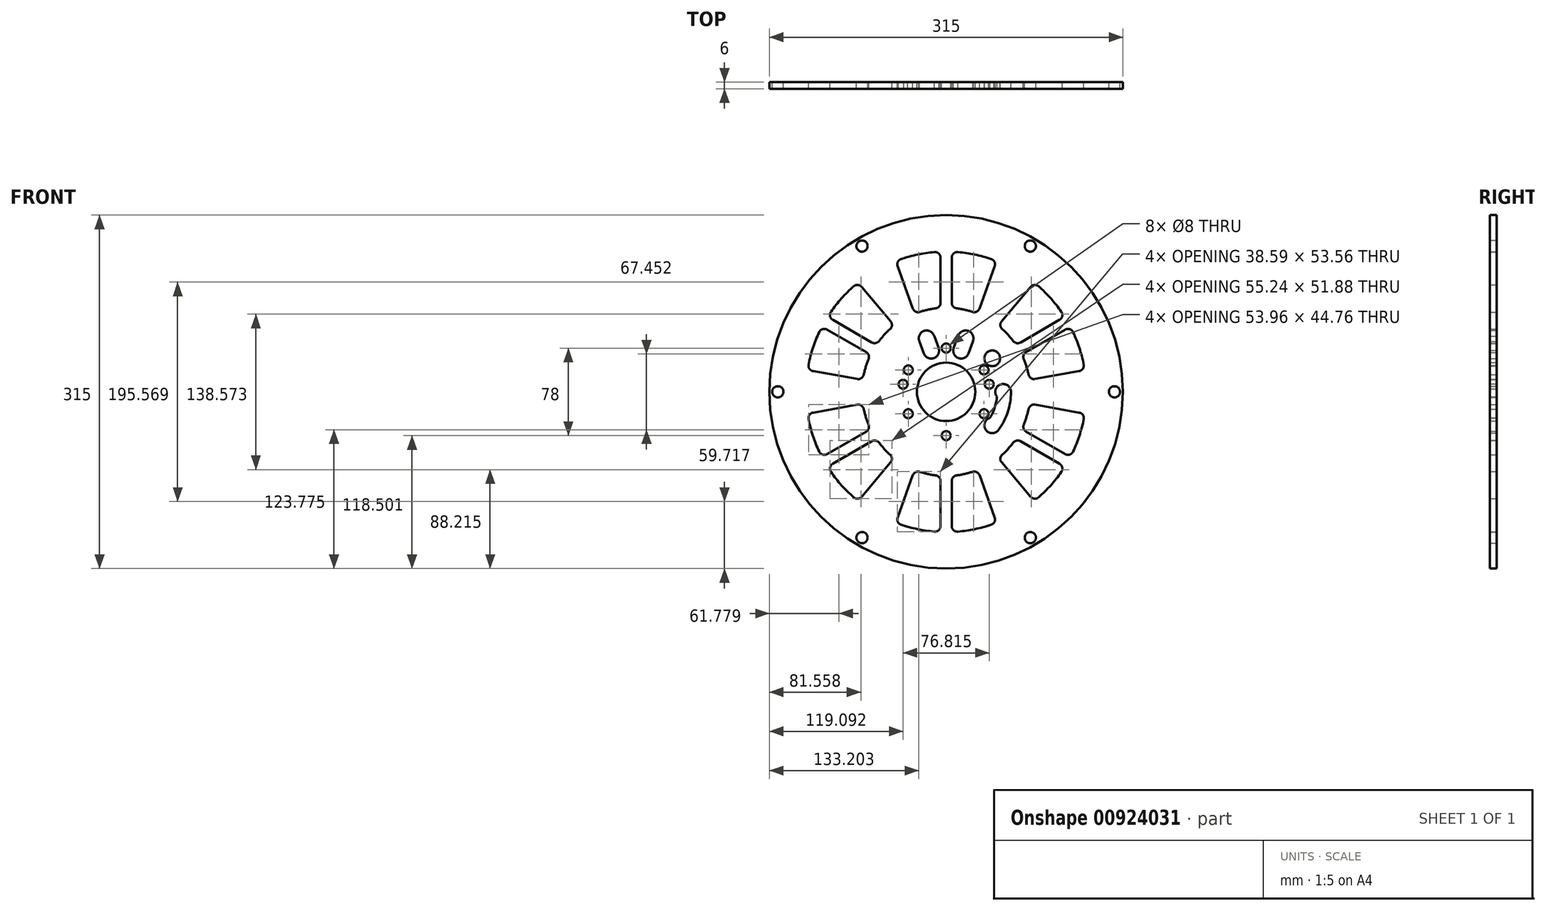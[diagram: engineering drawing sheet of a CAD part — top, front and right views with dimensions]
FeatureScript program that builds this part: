
annotation { "Feature Type Name" : "Feature", "Feature Type Description" : "" }
export const myFeature = defineFeature(function(context is Context, id is Id, definition is map)
    precondition{}
    {
        {
            var Q0;
            Q0=qCreatedBy(makeId("Front.planeOp"),FACE);
            var sketch = newSketch(context, id + "F0", { "sketchPlane" : qUnion([Q0])});
            skCircle(sketch, "E0", {"center": v(-91.13, 167.67) * mm, "radius": 15 * mm, "construction": true});
            skCircle(sketch, "E1", {"center": v(-91.13, 167.67) * mm, "radius": 26 * mm});
            skCircle(sketch, "E2", {"center": v(-91.13, 167.67) * mm, "radius": 39 * mm, "construction": true});
            skCircle(sketch, "E3", {"center": v(-91.13, 167.67) * mm, "radius": 62.5 * mm, "construction": true});
            skCircle(sketch, "E4", {"center": v(-91.13, 167.67) * mm, "radius": 140 * mm, "construction": true});
            skCircle(sketch, "E5", {"center": v(-40.38, 167.67) * mm, "radius": 4.86 * mm, "construction": true});
            skLineSegment(sketch, "E6", {"start": v(-52.13, 167.67) * mm, "end": v(-28.63, 167.67) * mm, "construction": true});
            skCircle(sketch, "E7", {"center": v(-91.13, 167.67) * mm, "radius": 50.75 * mm, "construction": true});
            skCircle(sketch, "E8.1.0", {"center": v(-42.86, 183.35) * mm, "radius": 4.86 * mm, "construction": true});
            skCircle(sketch, "E8.2.0", {"center": v(-50.07, 197.5) * mm, "radius": 4.86 * mm, "construction": true});
            skCircle(sketch, "E8.3.0", {"center": v(-61.3, 208.73) * mm, "radius": 4.86 * mm, "construction": true});
            skCircle(sketch, "E8.4.0", {"center": v(-75.45, 215.94) * mm, "radius": 4.86 * mm, "construction": true});
            skCircle(sketch, "E8.5.0", {"center": v(-91.13, 218.42) * mm, "radius": 4.86 * mm, "construction": true});
            skCircle(sketch, "E8.6.0", {"center": v(-106.81, 215.94) * mm, "radius": 4.86 * mm, "construction": true});
            skCircle(sketch, "E8.7.0", {"center": v(-120.96, 208.73) * mm, "radius": 4.86 * mm, "construction": true});
            skCircle(sketch, "E8.8.0", {"center": v(-132.19, 197.5) * mm, "radius": 4.86 * mm, "construction": true});
            skCircle(sketch, "E8.9.0", {"center": v(-139.4, 183.35) * mm, "radius": 4.86 * mm, "construction": true});
            skCircle(sketch, "E8.10.0", {"center": v(-141.88, 167.67) * mm, "radius": 4.86 * mm, "construction": true});
            skCircle(sketch, "E8.11.0", {"center": v(-139.4, 151.99) * mm, "radius": 4.86 * mm, "construction": true});
            skCircle(sketch, "E8.12.0", {"center": v(-132.19, 137.84) * mm, "radius": 4.86 * mm, "construction": true});
            skCircle(sketch, "E8.13.0", {"center": v(-120.96, 126.61) * mm, "radius": 4.86 * mm, "construction": true});
            skCircle(sketch, "E8.14.0", {"center": v(-106.81, 119.4) * mm, "radius": 4.86 * mm, "construction": true});
            skCircle(sketch, "E8.15.0", {"center": v(-91.13, 116.92) * mm, "radius": 4.86 * mm, "construction": true});
            skCircle(sketch, "E8.16.0", {"center": v(-75.45, 119.4) * mm, "radius": 4.86 * mm, "construction": true});
            skCircle(sketch, "E8.17.0", {"center": v(-61.3, 126.61) * mm, "radius": 4.86 * mm, "construction": true});
            skCircle(sketch, "E8.18.0", {"center": v(-50.07, 137.84) * mm, "radius": 4.86 * mm, "construction": true});
            skCircle(sketch, "E8.19.0", {"center": v(-42.86, 151.99) * mm, "radius": 4.86 * mm, "construction": true});
            skCircle(sketch, "E9", {"center": v(-50.07, 197.5) * mm, "radius": 7 * mm});
            skArc(sketch, "E10", {"start": v(-33.38, 167.67) * mm, "mid": v(-42.7, 174.28) * mm, "end": v(-45.84, 163.3) * mm});
            skArc(sketch, "E11", {"start": v(-51.92, 144.6) * mm, "mid": v(-55.83, 133.86) * mm, "end": v(-44.4, 133.73) * mm});
            skCircle(sketch, "E12", {"center": v(-91.13, 167.67) * mm, "radius": 157.5 * mm});
            skCircle(sketch, "E13", {"center": v(-91.13, 167.67) * mm, "radius": 150 * mm, "construction": true});
            skCircle(sketch, "E14", {"center": v(58.87, 167.67) * mm, "radius": 5 * mm});
            skCircle(sketch, "E15.1.0", {"center": v(-16.13, 297.58) * mm, "radius": 5 * mm});
            skCircle(sketch, "E15.2.0", {"center": v(-166.13, 297.58) * mm, "radius": 5 * mm});
            skCircle(sketch, "E15.3.0", {"center": v(-241.13, 167.67) * mm, "radius": 5 * mm});
            skCircle(sketch, "E15.4.0", {"center": v(-166.13, 37.77) * mm, "radius": 5 * mm});
            skCircle(sketch, "E15.5.0", {"center": v(-16.13, 37.77) * mm, "radius": 5 * mm});
            skCircle(sketch, "E16", {"center": v(-91.13, 206.67) * mm, "radius": 4 * mm});
            skCircle(sketch, "E17.1.0", {"center": v(-104.47, 204.32) * mm, "radius": 4 * mm, "construction": true});
            skCircle(sketch, "E17.2.0", {"center": v(-116.2, 197.55) * mm, "radius": 4 * mm, "construction": true});
            skCircle(sketch, "E17.3.0", {"center": v(-124.9, 187.17) * mm, "radius": 4 * mm});
            skCircle(sketch, "E17.4.0", {"center": v(-129.54, 174.44) * mm, "radius": 4 * mm});
            skCircle(sketch, "E17.5.0", {"center": v(-129.54, 160.9) * mm, "radius": 4 * mm, "construction": true});
            skCircle(sketch, "E17.6.0", {"center": v(-124.9, 148.17) * mm, "radius": 4 * mm});
            skCircle(sketch, "E17.7.0", {"center": v(-116.2, 137.8) * mm, "radius": 4 * mm, "construction": true});
            skCircle(sketch, "E17.8.0", {"center": v(-104.47, 131.02) * mm, "radius": 4 * mm, "construction": true});
            skCircle(sketch, "E17.9.0", {"center": v(-91.13, 128.67) * mm, "radius": 4 * mm});
            skCircle(sketch, "E17.10.0", {"center": v(-77.8, 131.02) * mm, "radius": 4 * mm, "construction": true});
            skCircle(sketch, "E17.11.0", {"center": v(-66.06, 137.8) * mm, "radius": 4 * mm, "construction": true});
            skCircle(sketch, "E17.12.0", {"center": v(-57.36, 148.17) * mm, "radius": 4 * mm});
            skCircle(sketch, "E17.13.0", {"center": v(-52.72, 160.9) * mm, "radius": 4 * mm, "construction": true});
            skCircle(sketch, "E17.14.0", {"center": v(-52.72, 174.44) * mm, "radius": 4 * mm});
            skCircle(sketch, "E17.15.0", {"center": v(-57.36, 187.17) * mm, "radius": 4 * mm});
            skCircle(sketch, "E17.16.0", {"center": v(-66.06, 197.55) * mm, "radius": 4 * mm, "construction": true});
            skCircle(sketch, "E17.17.0", {"center": v(-77.8, 204.32) * mm, "radius": 4 * mm, "construction": true});
            skArc(sketch, "E18", {"start": v(-105.73, 211.2) * mm, "mid": v(-105.85, 211.18) * mm, "end": v(-105.98, 211.15) * mm});
            skCircle(sketch, "E19", {"center": v(-91.13, 167.67) * mm, "radius": 134 * mm, "construction": true});
            skArc(sketch, "E20", {"start": v(-50.92, 49.31) * mm, "mid": v(-91.13, 292.67) * mm, "end": v(-131.34, 49.31) * mm, "construction": true});
            skCircle(sketch, "E21", {"center": v(-91.13, 167.67) * mm, "radius": 75 * mm, "construction": true});
            skLineSegment(sketch, "E22", {"start": v(-304.88, 167.67) * mm, "end": v(220.89, 167.67) * mm, "construction": true});
            skLineSegment(sketch, "E23", {"start": v(-166.13, 37.77) * mm, "end": v(-16.13, 297.58) * mm, "construction": true});
            skLineSegment(sketch, "E24", {"start": v(-166.13, 297.58) * mm, "end": v(-16.13, 37.77) * mm, "construction": true});
            skArc(sketch, "E25", {"start": v(-114.57, 96.43) * mm, "mid": v(-107.61, 94.5) * mm, "end": v(-100.5, 93.26) * mm});
            skArc(sketch, "E26", {"start": v(-131.34, 49.31) * mm, "mid": v(-116.63, 45.3) * mm, "end": v(-101.55, 43.1) * mm});
            skLineSegment(sketch, "E27", {"start": v(-120.83, 93.38) * mm, "end": v(-134.43, 55.75) * mm});
            skLineSegment(sketch, "E28", {"start": v(-61.43, 93.38) * mm, "end": v(-47.83, 55.75) * mm});
            skLineSegment(sketch, "E29", {"start": v(-91.13, 42.67) * mm, "end": v(-91.13, 92.67) * mm, "construction": true});
            skLineSegment(sketch, "E30", {"start": v(-86.13, 88.3) * mm, "end": v(-86.13, 48.09) * mm});
            skLineSegment(sketch, "E31", {"start": v(-96.13, 88.3) * mm, "end": v(-96.13, 48.09) * mm});
            skArc(sketch, "E32.trimOffspring", {"start": v(-81.76, 93.26) * mm, "mid": v(-74.65, 94.5) * mm, "end": v(-67.7, 96.43) * mm});
            skArc(sketch, "E33.trimOffspring", {"start": v(-80.71, 43.1) * mm, "mid": v(-65.63, 45.3) * mm, "end": v(-50.92, 49.31) * mm});
            skPoint(sketch, "E34.visualSharp", {"position": v(-46.13, 51.05) * mm});
            skArc(sketch, "E34.filletArc", {"start": v(-50.92, 49.31) * mm, "mid": v(-48.02, 51.88) * mm, "end": v(-47.83, 55.75) * mm});
            skPoint(sketch, "E35.visualSharp", {"position": v(-63.13, 98.1) * mm});
            skArc(sketch, "E35.filletArc", {"start": v(-61.43, 93.38) * mm, "mid": v(-63.94, 96.17) * mm, "end": v(-67.7, 96.43) * mm});
            skPoint(sketch, "E36.visualSharp", {"position": v(-119.13, 98.1) * mm});
            skArc(sketch, "E36.filletArc", {"start": v(-114.57, 96.43) * mm, "mid": v(-118.32, 96.17) * mm, "end": v(-120.83, 93.38) * mm});
            skPoint(sketch, "E37.visualSharp", {"position": v(-136.13, 51.05) * mm});
            skArc(sketch, "E37.filletArc", {"start": v(-134.43, 55.75) * mm, "mid": v(-134.24, 51.88) * mm, "end": v(-131.34, 49.31) * mm});
            skPoint(sketch, "E38.visualSharp", {"position": v(-96.13, 92.84) * mm});
            skArc(sketch, "E38.filletArc", {"start": v(-96.13, 88.3) * mm, "mid": v(-97.38, 91.6) * mm, "end": v(-100.5, 93.26) * mm});
            skPoint(sketch, "E39.visualSharp", {"position": v(-96.13, 42.77) * mm});
            skArc(sketch, "E39.filletArc", {"start": v(-101.55, 43.1) * mm, "mid": v(-97.75, 44.4) * mm, "end": v(-96.13, 48.09) * mm});
            skPoint(sketch, "E40.visualSharp", {"position": v(-86.13, 42.77) * mm});
            skArc(sketch, "E40.filletArc", {"start": v(-86.13, 48.09) * mm, "mid": v(-84.52, 44.4) * mm, "end": v(-80.71, 43.1) * mm});
            skPoint(sketch, "E41.visualSharp", {"position": v(-86.13, 92.84) * mm});
            skArc(sketch, "E41.filletArc", {"start": v(-81.76, 93.26) * mm, "mid": v(-84.88, 91.6) * mm, "end": v(-86.13, 88.3) * mm});
            skArc(sketch, "E42.trimOffspring", {"start": v(-101.55, 43.1) * mm, "mid": v(-91.13, 42.67) * mm, "end": v(-80.71, 43.1) * mm, "construction": true});
            skArc(sketch, "E43.1.0", {"start": v(-41.15, 111.75) * mm, "mid": v(-36, 116.81) * mm, "end": v(-31.38, 122.35) * mm});
            skArc(sketch, "E43.1.1", {"start": v(-22, 138.58) * mm, "mid": v(-19.52, 145.36) * mm, "end": v(-17.71, 152.35) * mm});
            skArc(sketch, "E43.1.2", {"start": v(-11.94, 156.25) * mm, "mid": v(-15.62, 155.47) * mm, "end": v(-17.71, 152.35) * mm});
            skArc(sketch, "E43.1.3", {"start": v(-22, 138.58) * mm, "mid": v(-22.13, 135.05) * mm, "end": v(-19.9, 132.32) * mm});
            skArc(sketch, "E43.1.4", {"start": v(-24.9, 123.66) * mm, "mid": v(-28.38, 124.23) * mm, "end": v(-31.38, 122.35) * mm});
            skLineSegment(sketch, "E43.1.5", {"start": v(-24.9, 123.66) * mm, "end": v(9.93, 103.55) * mm});
            skLineSegment(sketch, "E43.1.6", {"start": v(-41.64, 104.8) * mm, "end": v(-15.85, 74.2) * mm});
            skArc(sketch, "E43.1.7", {"start": v(-41.15, 111.75) * mm, "mid": v(-42.8, 108.37) * mm, "end": v(-41.64, 104.8) * mm});
            skArc(sketch, "E43.1.8", {"start": v(-15.85, 74.2) * mm, "mid": v(-12.4, 72.45) * mm, "end": v(-8.73, 73.67) * mm});
            skArc(sketch, "E43.1.9", {"start": v(-8.73, 73.67) * mm, "mid": v(2.1, 84.4) * mm, "end": v(11.54, 96.37) * mm});
            skArc(sketch, "E43.1.10", {"start": v(11.54, 96.37) * mm, "mid": v(12.31, 100.31) * mm, "end": v(9.93, 103.55) * mm});
            skArc(sketch, "E43.1.11", {"start": v(14.93, 112.21) * mm, "mid": v(18.93, 111.77) * mm, "end": v(21.95, 114.4) * mm});
            skLineSegment(sketch, "E43.1.12", {"start": v(-19.9, 132.32) * mm, "end": v(14.93, 112.21) * mm});
            skArc(sketch, "E43.1.13", {"start": v(21.95, 114.4) * mm, "mid": v(27.6, 128.57) * mm, "end": v(31.47, 143.32) * mm});
            skLineSegment(sketch, "E43.1.14", {"start": v(-11.94, 156.25) * mm, "end": v(27.45, 149.21) * mm});
            skArc(sketch, "E43.1.15", {"start": v(31.47, 143.32) * mm, "mid": v(30.7, 147.1) * mm, "end": v(27.45, 149.21) * mm});
            skArc(sketch, "E43.2.0", {"start": v(-17.71, 183) * mm, "mid": v(-19.52, 189.98) * mm, "end": v(-22, 196.76) * mm});
            skArc(sketch, "E43.2.1", {"start": v(-31.38, 213) * mm, "mid": v(-36, 218.53) * mm, "end": v(-41.15, 223.6) * mm});
            skArc(sketch, "E43.2.2", {"start": v(-41.64, 230.54) * mm, "mid": v(-42.8, 226.97) * mm, "end": v(-41.15, 223.6) * mm});
            skArc(sketch, "E43.2.3", {"start": v(-31.38, 213) * mm, "mid": v(-28.38, 211.12) * mm, "end": v(-24.9, 211.69) * mm});
            skArc(sketch, "E43.2.4", {"start": v(-19.9, 203.03) * mm, "mid": v(-22.13, 200.3) * mm, "end": v(-22, 196.76) * mm});
            skLineSegment(sketch, "E43.2.5", {"start": v(-19.9, 203.03) * mm, "end": v(14.93, 223.13) * mm});
            skLineSegment(sketch, "E43.2.6", {"start": v(-11.94, 179.1) * mm, "end": v(27.45, 186.13) * mm});
            skArc(sketch, "E43.2.7", {"start": v(-17.71, 183) * mm, "mid": v(-15.62, 179.87) * mm, "end": v(-11.94, 179.1) * mm});
            skArc(sketch, "E43.2.8", {"start": v(27.45, 186.13) * mm, "mid": v(30.7, 188.23) * mm, "end": v(31.47, 192.03) * mm});
            skArc(sketch, "E43.2.9", {"start": v(31.47, 192.03) * mm, "mid": v(27.6, 206.77) * mm, "end": v(21.95, 220.93) * mm});
            skArc(sketch, "E43.2.10", {"start": v(21.95, 220.93) * mm, "mid": v(18.93, 223.57) * mm, "end": v(14.93, 223.13) * mm});
            skArc(sketch, "E43.2.11", {"start": v(9.93, 231.8) * mm, "mid": v(12.31, 235.03) * mm, "end": v(11.54, 238.98) * mm});
            skLineSegment(sketch, "E43.2.12", {"start": v(-24.9, 211.69) * mm, "end": v(9.93, 231.8) * mm});
            skArc(sketch, "E43.2.13", {"start": v(11.54, 238.98) * mm, "mid": v(2.1, 250.94) * mm, "end": v(-8.73, 261.67) * mm});
            skLineSegment(sketch, "E43.2.14", {"start": v(-41.64, 230.54) * mm, "end": v(-15.85, 261.13) * mm});
            skArc(sketch, "E43.2.15", {"start": v(-8.73, 261.67) * mm, "mid": v(-12.4, 262.9) * mm, "end": v(-15.85, 261.13) * mm});
            skArc(sketch, "E43.3.0", {"start": v(-67.7, 238.91) * mm, "mid": v(-74.65, 240.84) * mm, "end": v(-81.76, 242.08) * mm});
            skArc(sketch, "E43.3.1", {"start": v(-100.5, 242.08) * mm, "mid": v(-107.61, 240.84) * mm, "end": v(-114.57, 238.91) * mm});
            skArc(sketch, "E43.3.2", {"start": v(-120.83, 241.96) * mm, "mid": v(-118.32, 239.17) * mm, "end": v(-114.57, 238.91) * mm});
            skArc(sketch, "E43.3.3", {"start": v(-100.5, 242.08) * mm, "mid": v(-97.38, 243.74) * mm, "end": v(-96.13, 247.04) * mm});
            skArc(sketch, "E43.3.4", {"start": v(-86.13, 247.04) * mm, "mid": v(-84.88, 243.74) * mm, "end": v(-81.76, 242.08) * mm});
            skLineSegment(sketch, "E43.3.5", {"start": v(-86.13, 247.04) * mm, "end": v(-86.13, 287.25) * mm});
            skLineSegment(sketch, "E43.3.6", {"start": v(-61.43, 241.96) * mm, "end": v(-47.83, 279.6) * mm});
            skArc(sketch, "E43.3.7", {"start": v(-67.7, 238.91) * mm, "mid": v(-63.94, 239.17) * mm, "end": v(-61.43, 241.96) * mm});
            skArc(sketch, "E43.3.8", {"start": v(-47.83, 279.6) * mm, "mid": v(-48.02, 283.46) * mm, "end": v(-50.92, 286.03) * mm});
            skArc(sketch, "E43.3.9", {"start": v(-50.92, 286.03) * mm, "mid": v(-65.63, 290.04) * mm, "end": v(-80.71, 292.24) * mm});
            skArc(sketch, "E43.3.10", {"start": v(-80.71, 292.24) * mm, "mid": v(-84.52, 290.93) * mm, "end": v(-86.13, 287.25) * mm});
            skArc(sketch, "E43.3.11", {"start": v(-96.13, 287.25) * mm, "mid": v(-97.75, 290.93) * mm, "end": v(-101.55, 292.24) * mm});
            skLineSegment(sketch, "E43.3.12", {"start": v(-96.13, 247.04) * mm, "end": v(-96.13, 287.25) * mm});
            skArc(sketch, "E43.3.13", {"start": v(-101.55, 292.24) * mm, "mid": v(-116.63, 290.04) * mm, "end": v(-131.34, 286.03) * mm});
            skLineSegment(sketch, "E43.3.14", {"start": v(-120.83, 241.96) * mm, "end": v(-134.43, 279.6) * mm});
            skArc(sketch, "E43.3.15", {"start": v(-131.34, 286.03) * mm, "mid": v(-134.24, 283.46) * mm, "end": v(-134.43, 279.6) * mm});
            skArc(sketch, "E43.4.0", {"start": v(-141.1, 223.6) * mm, "mid": v(-146.25, 218.53) * mm, "end": v(-150.89, 213) * mm});
            skArc(sketch, "E43.4.1", {"start": v(-160.26, 196.76) * mm, "mid": v(-162.74, 189.98) * mm, "end": v(-164.55, 183) * mm});
            skArc(sketch, "E43.4.2", {"start": v(-170.32, 179.1) * mm, "mid": v(-166.64, 179.87) * mm, "end": v(-164.55, 183) * mm});
            skArc(sketch, "E43.4.3", {"start": v(-160.26, 196.76) * mm, "mid": v(-160.13, 200.3) * mm, "end": v(-162.37, 203.03) * mm});
            skArc(sketch, "E43.4.4", {"start": v(-157.37, 211.69) * mm, "mid": v(-153.88, 211.12) * mm, "end": v(-150.89, 213) * mm});
            skLineSegment(sketch, "E43.4.5", {"start": v(-157.37, 211.69) * mm, "end": v(-192.2, 231.8) * mm});
            skLineSegment(sketch, "E43.4.6", {"start": v(-140.62, 230.54) * mm, "end": v(-166.4, 261.13) * mm});
            skArc(sketch, "E43.4.7", {"start": v(-141.1, 223.6) * mm, "mid": v(-139.45, 226.97) * mm, "end": v(-140.62, 230.54) * mm});
            skArc(sketch, "E43.4.8", {"start": v(-166.4, 261.13) * mm, "mid": v(-169.85, 262.9) * mm, "end": v(-173.53, 261.67) * mm});
            skArc(sketch, "E43.4.9", {"start": v(-173.53, 261.67) * mm, "mid": v(-184.36, 250.94) * mm, "end": v(-193.8, 238.98) * mm});
            skArc(sketch, "E43.4.10", {"start": v(-193.8, 238.98) * mm, "mid": v(-194.57, 235.03) * mm, "end": v(-192.2, 231.8) * mm});
            skArc(sketch, "E43.4.11", {"start": v(-197.2, 223.13) * mm, "mid": v(-201.19, 223.57) * mm, "end": v(-204.22, 220.93) * mm});
            skLineSegment(sketch, "E43.4.12", {"start": v(-162.37, 203.03) * mm, "end": v(-197.2, 223.13) * mm});
            skArc(sketch, "E43.4.13", {"start": v(-204.22, 220.93) * mm, "mid": v(-209.86, 206.77) * mm, "end": v(-213.73, 192.03) * mm});
            skLineSegment(sketch, "E43.4.14", {"start": v(-170.32, 179.1) * mm, "end": v(-209.7, 186.13) * mm});
            skArc(sketch, "E43.4.15", {"start": v(-213.73, 192.03) * mm, "mid": v(-212.96, 188.23) * mm, "end": v(-209.7, 186.13) * mm});
            skArc(sketch, "E43.5.0", {"start": v(-164.55, 152.35) * mm, "mid": v(-162.74, 145.36) * mm, "end": v(-160.26, 138.58) * mm});
            skArc(sketch, "E43.5.1", {"start": v(-150.89, 122.35) * mm, "mid": v(-146.25, 116.81) * mm, "end": v(-141.1, 111.75) * mm});
            skArc(sketch, "E43.5.2", {"start": v(-140.62, 104.8) * mm, "mid": v(-139.45, 108.37) * mm, "end": v(-141.1, 111.75) * mm});
            skArc(sketch, "E43.5.3", {"start": v(-150.89, 122.35) * mm, "mid": v(-153.88, 124.23) * mm, "end": v(-157.37, 123.66) * mm});
            skArc(sketch, "E43.5.4", {"start": v(-162.37, 132.32) * mm, "mid": v(-160.13, 135.05) * mm, "end": v(-160.26, 138.58) * mm});
            skLineSegment(sketch, "E43.5.5", {"start": v(-162.37, 132.32) * mm, "end": v(-197.2, 112.21) * mm});
            skLineSegment(sketch, "E43.5.6", {"start": v(-170.32, 156.25) * mm, "end": v(-209.7, 149.21) * mm});
            skArc(sketch, "E43.5.7", {"start": v(-164.55, 152.35) * mm, "mid": v(-166.64, 155.47) * mm, "end": v(-170.32, 156.25) * mm});
            skArc(sketch, "E43.5.8", {"start": v(-209.7, 149.21) * mm, "mid": v(-212.96, 147.1) * mm, "end": v(-213.73, 143.32) * mm});
            skArc(sketch, "E43.5.9", {"start": v(-213.73, 143.32) * mm, "mid": v(-209.86, 128.57) * mm, "end": v(-204.22, 114.4) * mm});
            skArc(sketch, "E43.5.10", {"start": v(-204.22, 114.4) * mm, "mid": v(-201.19, 111.77) * mm, "end": v(-197.2, 112.21) * mm});
            skArc(sketch, "E43.5.11", {"start": v(-192.2, 103.55) * mm, "mid": v(-194.57, 100.31) * mm, "end": v(-193.8, 96.37) * mm});
            skLineSegment(sketch, "E43.5.12", {"start": v(-157.37, 123.66) * mm, "end": v(-192.2, 103.55) * mm});
            skArc(sketch, "E43.5.13", {"start": v(-193.8, 96.37) * mm, "mid": v(-184.36, 84.4) * mm, "end": v(-173.53, 73.67) * mm});
            skLineSegment(sketch, "E43.5.14", {"start": v(-140.62, 104.8) * mm, "end": v(-166.4, 74.2) * mm});
            skArc(sketch, "E43.5.15", {"start": v(-173.53, 73.67) * mm, "mid": v(-169.85, 72.45) * mm, "end": v(-166.4, 74.2) * mm});
            skCircle(sketch, "E44", {"center": v(-91.13, 167.67) * mm, "radius": 45.5 * mm, "construction": true});
            skArc(sketch, "E45", {"start": v(-51.92, 144.6) * mm, "mid": v(-47.86, 153.61) * mm, "end": v(-45.84, 163.3) * mm});
            skArc(sketch, "E46", {"start": v(-33.38, 167.67) * mm, "mid": v(-36.2, 149.83) * mm, "end": v(-44.4, 133.73) * mm});
            skLineSegment(sketch, "E47", {"start": v(-91.13, 167.67) * mm, "end": v(-104.47, 204.32) * mm, "construction": true});
            skLineSegment(sketch, "E48", {"start": v(-100.82, 194.3) * mm, "end": v(-112.5, 226.4) * mm, "construction": true});
            skLineSegment(sketch, "E49", {"start": v(-91.13, 167.67) * mm, "end": v(-77.8, 204.32) * mm, "construction": true});
            skLineSegment(sketch, "E50", {"start": v(-81.45, 194.27) * mm, "end": v(-69.75, 226.4) * mm, "construction": true});
            skLineSegment(sketch, "E51", {"start": v(-80.5, 217.3) * mm, "end": v(-84.59, 206.12) * mm});
            skLineSegment(sketch, "E52", {"start": v(-67.38, 212.52) * mm, "end": v(-71.43, 201.33) * mm});
            skLineSegment(sketch, "E53", {"start": v(-101.76, 217.3) * mm, "end": v(-97.67, 206.12) * mm});
            skLineSegment(sketch, "E54", {"start": v(-114.88, 212.52) * mm, "end": v(-110.83, 201.33) * mm});
            skArc(sketch, "E55.trimOffspring", {"start": v(-111.22, 202.47) * mm, "mid": v(-102.34, 197.65) * mm, "end": v(-97.9, 206.72) * mm});
            skArc(sketch, "E56.trimOffspring", {"start": v(-101.76, 217.3) * mm, "mid": v(-110.88, 221.94) * mm, "end": v(-114.88, 212.52) * mm});
            skArc(sketch, "E57.trimOffspring", {"start": v(-67.38, 212.52) * mm, "mid": v(-71.38, 221.94) * mm, "end": v(-80.5, 217.3) * mm});
            skArc(sketch, "E58.trimOffspring", {"start": v(-84.37, 206.72) * mm, "mid": v(-79.92, 197.65) * mm, "end": v(-71.04, 202.47) * mm});
            skArc(sketch, "E59.trimOffspring", {"start": v(-76.28, 211.15) * mm, "mid": v(-76.4, 211.18) * mm, "end": v(-76.53, 211.2) * mm});
            skSolve(sketch);
        }
        {
            var Q0;
            Q0 = qSketchRegion(id + "F0", true);
            extrude(context, id + "F1", {"entities" : qUnion([Q0]), "depth" : 6 * mm, "offsetDistance" : 25 * mm});
        }
    });
